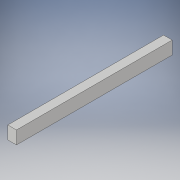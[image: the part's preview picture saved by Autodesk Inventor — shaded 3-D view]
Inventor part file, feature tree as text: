
AUTODESK INVENTOR PART (.ipt)
format: ipt  version: 2017 (Build 210142000, 142)  size: 91,136 bytes
history: native  units: in
note: dims shown in document units (in); Inventor stores cm internally (conversion verified against a paired STEP export)
features: extrude x1, sketch x1
ambient origin geometry x8: Origin, YZ Plane, XZ Plane, XY Plane, X Axis, Y Axis, Z Axis, Center Point
bodies: Solid1 (feature_tree)
feature tree (2):
  extrude  "Extrusion1"  Depth=36.0in
  sketch  "Sketch1"  dims[d0=3.0in d1=36.0in d2=2.0in d3=0.0in]
